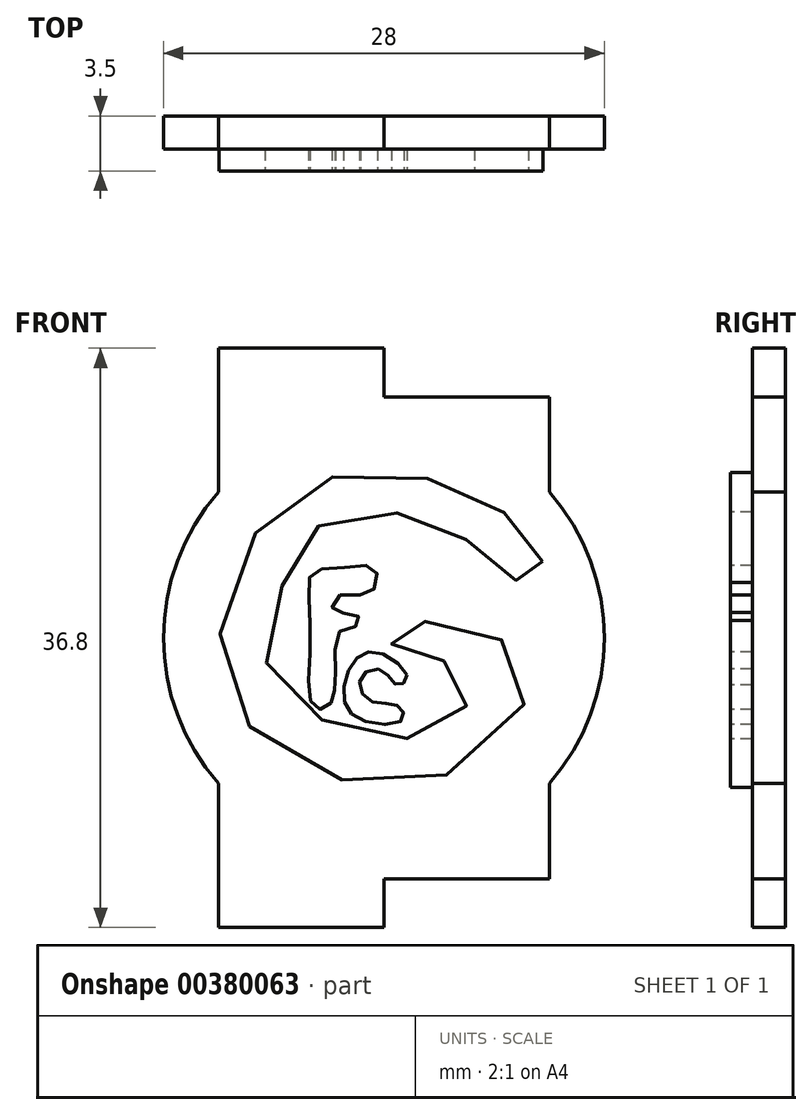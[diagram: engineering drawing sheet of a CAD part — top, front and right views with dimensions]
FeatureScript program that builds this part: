
annotation { "Feature Type Name" : "Feature", "Feature Type Description" : "" }
export const myFeature = defineFeature(function(context is Context, id is Id, definition is map)
    precondition{}
    {
        {
            var Q0;
            Q0=qCreatedBy(makeId("Front.planeOp"),FACE);
            var sketch = newSketch(context, id + "F0", { "sketchPlane" : qUnion([Q0])});
            skSolve(sketch);
        }
        {
            var Q0;
            Q0=qCreatedBy(makeId("Front.planeOp"),FACE);
            var sketch = newSketch(context, id + "F1", { "sketchPlane" : qUnion([Q0])});
            skArc(sketch, "E0", {"start": v(-10.5, 9.26) * mm, "mid": v(-14, 0) * mm, "end": v(-10.5, -9.26) * mm});
            skLineSegment(sketch, "E1", {"start": v(10.5, 9.26) * mm, "end": v(10.5, 15.3) * mm});
            skPoint(sketch, "E2.end.orphan", {"position": v(0, 16.84) * mm});
            skLineSegment(sketch, "E3", {"start": v(10.5, 15.3) * mm, "end": v(0, 15.3) * mm});
            skLineSegment(sketch, "E4", {"start": v(0, 15.3) * mm, "end": v(0, 18.4) * mm});
            skLineSegment(sketch, "E5", {"start": v(0, 18.4) * mm, "end": v(-10.5, 18.4) * mm});
            skLineSegment(sketch, "E6", {"start": v(-10.5, 18.4) * mm, "end": v(-10.5, 9.26) * mm});
            skLineSegment(sketch, "E7", {"start": v(-10.5, -9.26) * mm, "end": v(-10.5, -18.4) * mm});
            skLineSegment(sketch, "E8", {"start": v(-10.5, -18.4) * mm, "end": v(0, -18.4) * mm});
            skLineSegment(sketch, "E9", {"start": v(0, -18.4) * mm, "end": v(0, -15.3) * mm});
            skLineSegment(sketch, "E10", {"start": v(0, -15.3) * mm, "end": v(10.5, -15.3) * mm});
            skLineSegment(sketch, "E11", {"start": v(10.5, -15.3) * mm, "end": v(10.5, -9.26) * mm});
            skArc(sketch, "E12.trimOffspring", {"start": v(10.5, -9.26) * mm, "mid": v(14, 0) * mm, "end": v(10.5, 9.26) * mm});
            skSolve(sketch);
        }
        {
            var Q0;
            Q0=qCreatedBy(makeId("Front.planeOp"),FACE);
            var sketch = newSketch(context, id + "F2", { "sketchPlane" : qUnion([Q0])});
            skFitSpline(sketch, "E13", {"points": [v(10.06, 4.86) * mm, v(9.12, 6.65) * mm, v(5.63, 9.14) * mm, v(0.75, 10.44) * mm, v(-5.57, 9.34) * mm, v(-9.5, 3.77) * mm, v(-10.05, -3.35) * mm, v(-4.77, -8.18) * mm, v(2.5, -9.22) * mm, v(8.72, -4.65) * mm, v(8.52, -0.86) * mm, v(4.73, 0.63) * mm, v(1.6, 1.08) * mm, v(0.65, 0.43) * mm, v(0.65, -0.91) * mm, v(2.9, -1.36) * mm, v(5.68, -2.5) * mm, v(4.54, -5.2) * mm, v(1.7, -6.39) * mm, v(-3.28, -5.5) * mm, v(-7.11, -2.55) * mm, v(-7.31, 1.08) * mm, v(-5.47, 5.31) * mm, v(-3.78, 7.35) * mm, v(0.8, 7.95) * mm, v(4.54, 6.75) * mm, v(6.88, 4.71) * mm, v(8.92, 3.52) * mm, v(9.96, 3.92) * mm, v(10.06, 4.86) * mm]});
            skFitSpline(sketch, "E14", {"points": [v(-4.67, -4) * mm, v(-4.72, -1.31) * mm, v(-4.77, 2.57) * mm, v(-4.52, 4.17) * mm, v(-2.48, 4.46) * mm, v(-0.64, 4.46) * mm, v(-0.5, 3.32) * mm, v(-1.39, 2.72) * mm, v(-3.08, 2.57) * mm, v(-3.13, 1.63) * mm, v(-1.89, 1.58) * mm, v(-1.54, 0.88) * mm, v(-2.73, 0.48) * mm, v(-3.08, -1.4) * mm, v(-3.13, -3.3) * mm, v(-3.38, -4.15) * mm, v(-4.08, -4.55) * mm, v(-4.67, -4) * mm]});
            skFitSpline(sketch, "E15", {"points": [v(1.45, -2.36) * mm, v(0, -1.06) * mm, v(-1.44, -1.06) * mm, v(-2.38, -2.46) * mm, v(-2.43, -4.3) * mm, v(-1.09, -5.34) * mm, v(1.15, -5.24) * mm, v(1.15, -4.55) * mm, v(0.5, -4.2) * mm, v(-0.8, -4.05) * mm, v(-1.54, -3.1) * mm, v(-1.14, -2.16) * mm, v(0, -2.1) * mm, v(0.65, -2.9) * mm, v(1.2, -2.9) * mm, v(1.45, -2.36) * mm]});
            skSolve(sketch);
        }
        {
            var Q0;
            Q0 = qSketchRegion(id + "F0", true);
            var Q1;
            Q1 = qSketchRegion(id + "F1", true);
            extrude(context, id + "F3", {"entities" : qUnion([Q0, Q1]), "depth" : 2.1 * mm});
        }
        {
            var Q0;
            Q0 = qSketchRegion(id + "F2", true);
            extrude(context, id + "F4", {"entities" : qUnion([Q0]), "operationType" : NewBodyOperationType.ADD, "depth" : 3.5 * mm});
        }
    });
